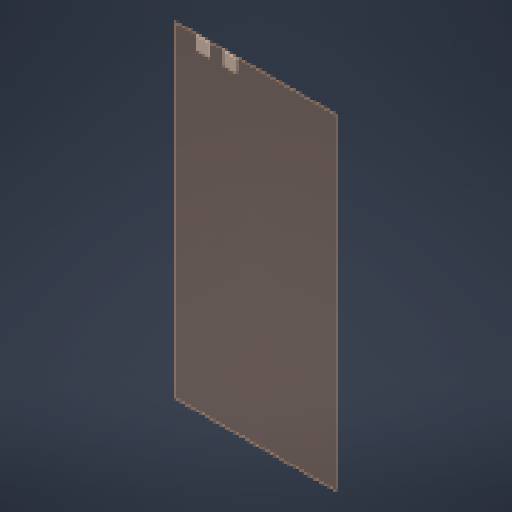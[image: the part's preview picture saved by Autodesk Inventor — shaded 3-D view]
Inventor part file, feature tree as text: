
AUTODESK INVENTOR PART (.ipt)
format: ipt  version: 2024 (Build 280153000, 153)  size: 128,512 bytes
history: native  units: mm
features: other x5, plane x1, extrude x1, sketch x1
ambient origin geometry x8: Origin, YZ Plane, XZ Plane, XY Plane, X Axis, Y Axis, Z Axis, Center Point
bodies: Body1 (feature_tree)
feature tree (8):
  other  "Sólido1"
  plane  "Plano de trabajo1"
  extrude  "Extrusión1"  Depth=30.0mm
  sketch  "Boceto1"  dims[d0=120.0mm d1=30.0mm d2=30.0mm d3=30.0mm d4=2.0mm d5=0.0mm]
  other  "<userpath>\Downloads\Piezas CMR\Marco_APM_002\Marco_apm_002-3.iam"
  other  "Marco_apm_002-3.iam"
  other  "Marco_Conveyor_Aereo:1"
  other  "Marco:1"
